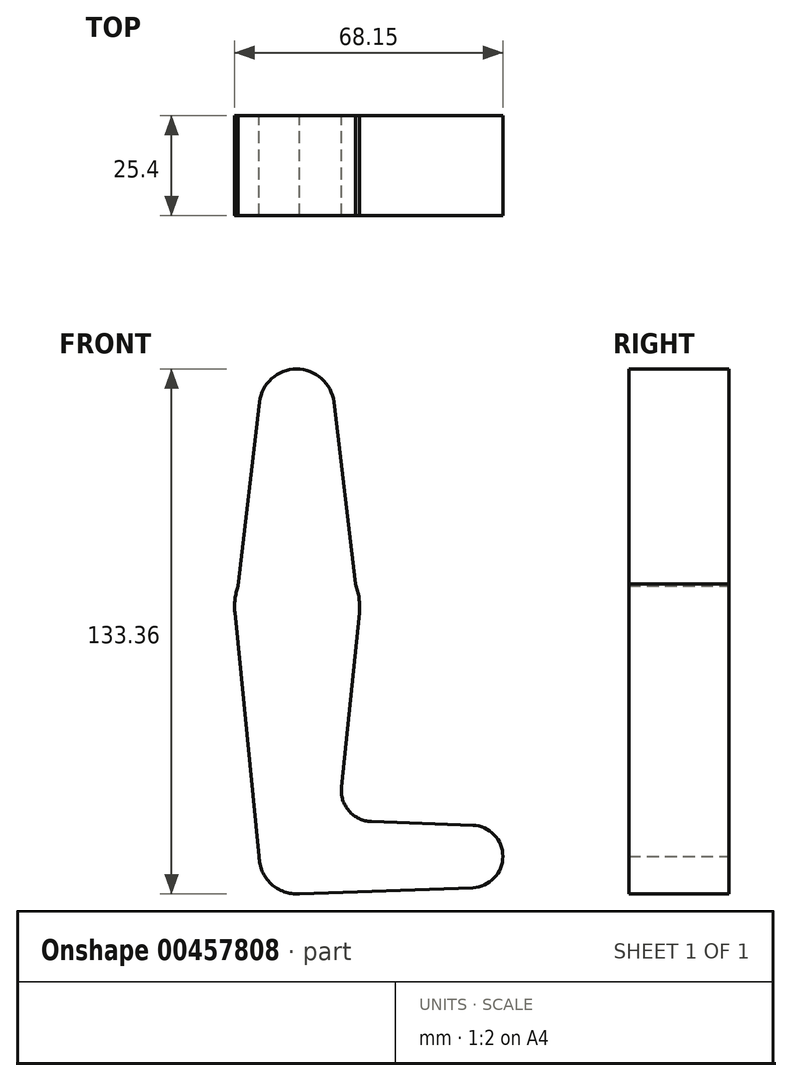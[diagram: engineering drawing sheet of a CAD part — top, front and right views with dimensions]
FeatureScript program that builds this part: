
annotation { "Feature Type Name" : "Feature", "Feature Type Description" : "" }
export const myFeature = defineFeature(function(context is Context, id is Id, definition is map)
    precondition{}
    {
        {
            var Q0;
            Q0=qCreatedBy(makeId("Front.planeOp"),FACE);
            var sketch = newSketch(context, id + "F0", { "sketchPlane" : qUnion([Q0])});
            skLineSegment(sketch, "E0", {"start": v(0, 0) * mm, "end": v(44.45, 0) * mm, "construction": true});
            skCircle(sketch, "E1", {"center": v(0, 114.3) * mm, "radius": 9.53 * mm});
            skCircle(sketch, "E2", {"center": v(0.11, 63.5) * mm, "radius": 15.88 * mm});
            skCircle(sketch, "E3", {"center": v(0, 0) * mm, "radius": 9.53 * mm});
            skCircle(sketch, "E4", {"center": v(44.45, 0) * mm, "radius": 7.94 * mm});
            skLineSegment(sketch, "E5", {"start": v(-9.46, 115.4) * mm, "end": v(-15.68, 61.91) * mm});
            skLineSegment(sketch, "E6", {"start": v(0, -9.53) * mm, "end": v(44.73, -7.93) * mm});
            skLineSegment(sketch, "E7.MirrorCS", {"start": v(9.46, 115.42) * mm, "end": v(15.8, 61.91) * mm});
            skLineSegment(sketch, "E8.MirrorCS", {"start": v(15.9, 61.91) * mm, "end": v(11.38, 17.6) * mm});
            skLineSegment(sketch, "E9.MirrorCS", {"start": v(19, 8.85) * mm, "end": v(44.73, 7.93) * mm});
            skPoint(sketch, "E10.newPointA", {"position": v(9.58, 0.01) * mm});
            skPoint(sketch, "E10.newPointB", {"position": v(0, 9.53) * mm});
            skArc(sketch, "E10.filletArc", {"start": v(11.38, 17.6) * mm, "mid": v(13.29, 11.57) * mm, "end": v(19, 8.85) * mm});
            skLineSegment(sketch, "E11", {"start": v(-9.52, 0) * mm, "end": v(-15.68, 61.93) * mm});
            skSolve(sketch);
        }
        {
            var Q0;
            Q0 = qSketchRegion(id + "F0", true);
            extrude(context, id + "F1", {"entities" : qUnion([Q0]), "depth" : 25.4 * mm});
        }
    });
